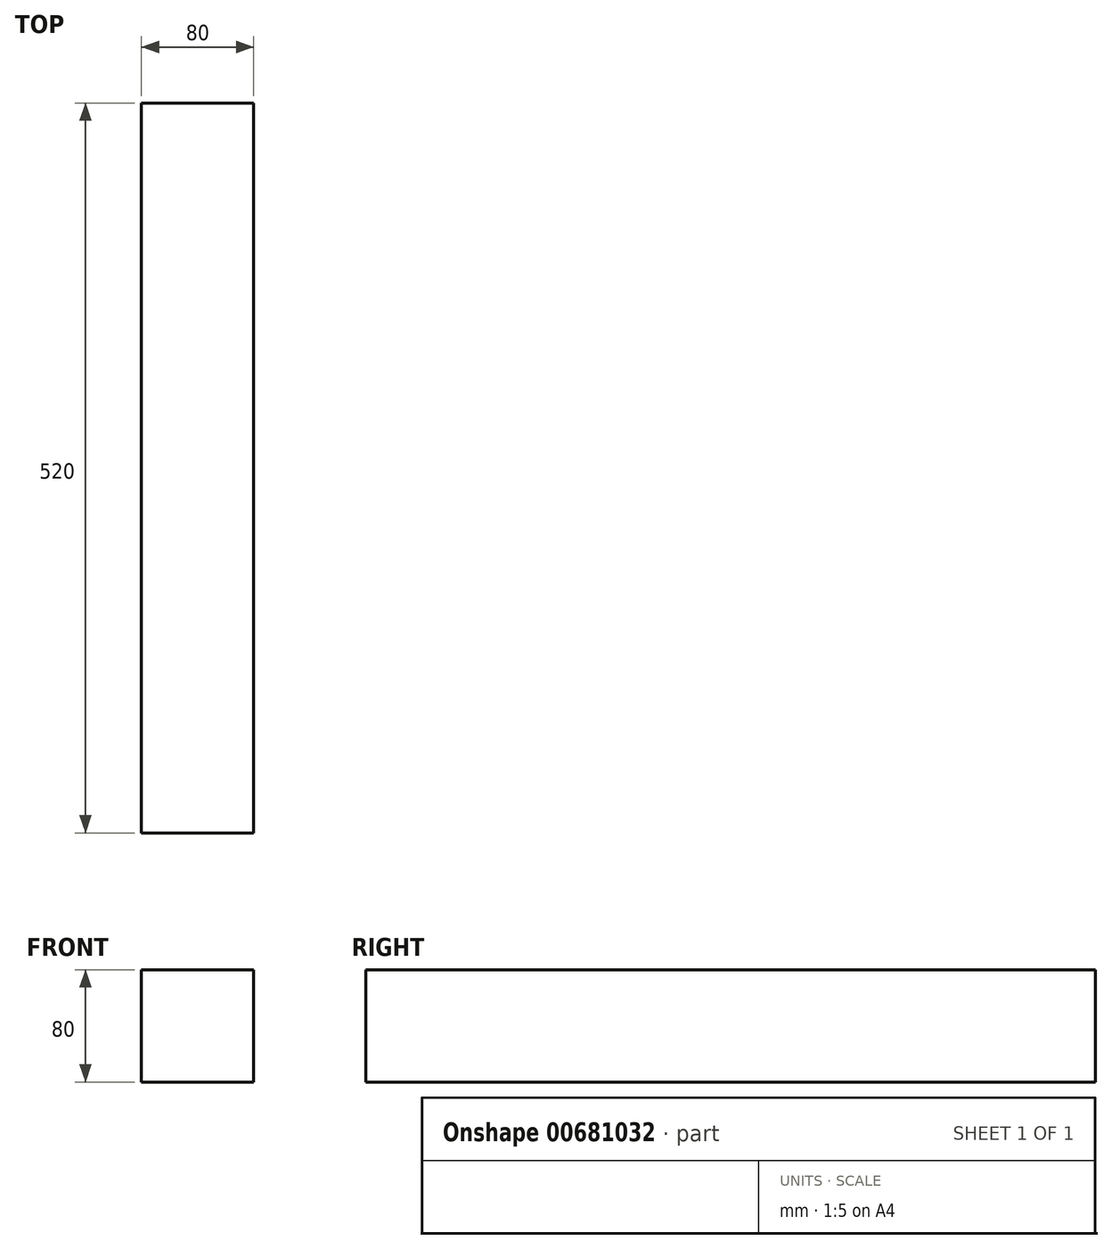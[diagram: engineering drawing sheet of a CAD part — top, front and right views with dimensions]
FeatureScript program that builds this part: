
annotation { "Feature Type Name" : "Feature", "Feature Type Description" : "" }
export const myFeature = defineFeature(function(context is Context, id is Id, definition is map)
    precondition{}
    {
        {
            var Q0;
            Q0=qCreatedBy(makeId("Front.planeOp"),FACE);
            var sketch = newSketch(context, id + "F0", { "sketchPlane" : qUnion([Q0])});
            skLineSegment(sketch, "E0.bottom", {"start": v(0, 0) * mm, "end": v(80, 0) * mm});
            skLineSegment(sketch, "E0.top", {"start": v(0, 80) * mm, "end": v(80, 80) * mm});
            skLineSegment(sketch, "E0.left", {"start": v(0, 0) * mm, "end": v(0, 80) * mm});
            skLineSegment(sketch, "E0.right", {"start": v(80, 0) * mm, "end": v(80, 80) * mm});
            skSolve(sketch);
        }
        {
            var Q0;
            Q0=makeQuery(id+"F0.imprint","IMPRINT",FACE,{"disambiguationData":[TD([[makeQuery(id+"F0.imprint","IMPRINT",EDGE,{"derivedFrom":sQuery(id+"F0.wireOp",EDGE,"E0.bottom")}),1.0]])]});
            extrude(context, id + "F1", {"entities" : qUnion([Q0]), "depth" : 520 * mm, "offsetDistance" : 25 * mm});
        }
    });
